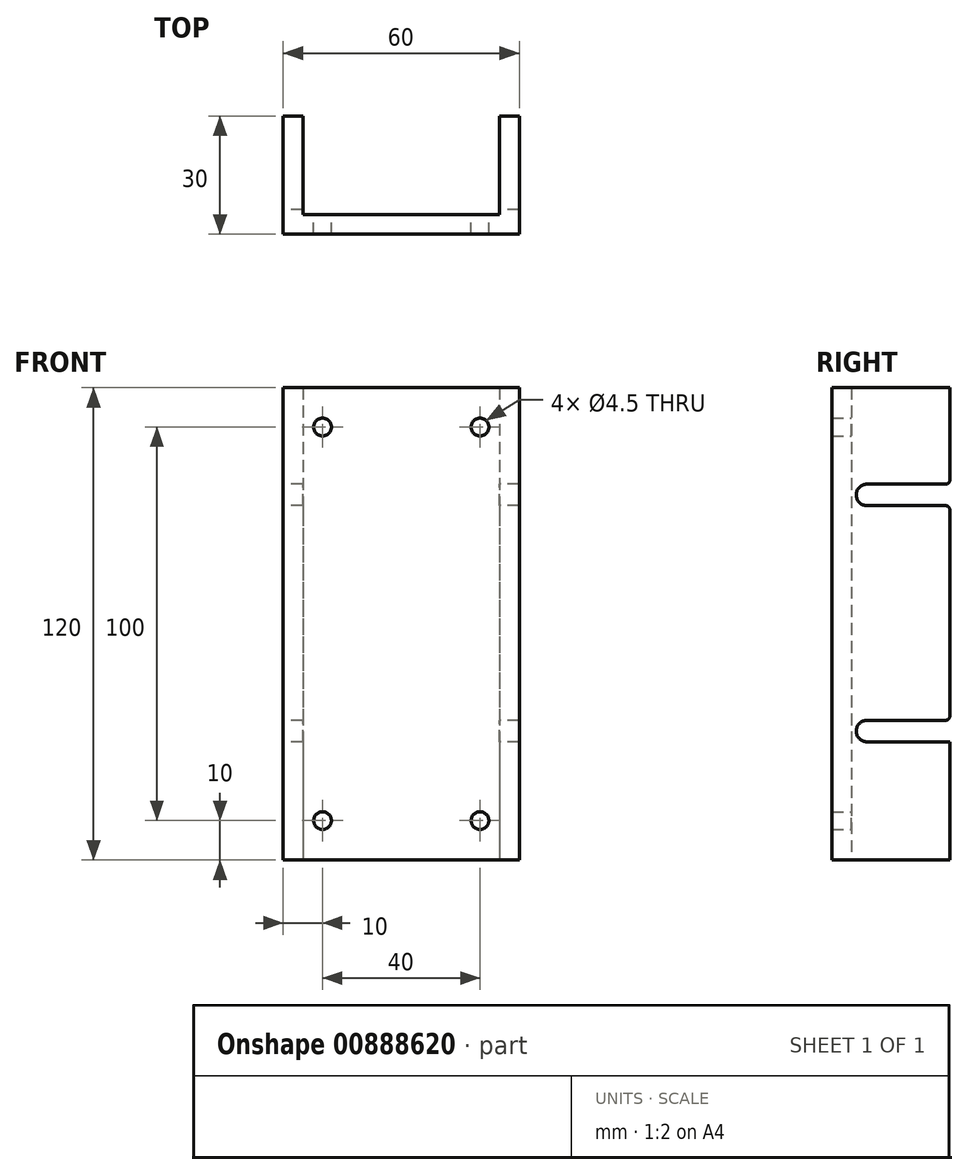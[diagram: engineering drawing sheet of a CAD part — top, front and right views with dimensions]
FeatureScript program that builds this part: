
annotation { "Feature Type Name" : "Feature", "Feature Type Description" : "" }
export const myFeature = defineFeature(function(context is Context, id is Id, definition is map)
    precondition{}
    {
        {
            var Q0;
            Q0=qCreatedBy(makeId("Front.planeOp"),FACE);
            var sketch = newSketch(context, id + "F0", { "sketchPlane" : qUnion([Q0])});
            skLineSegment(sketch, "E0.bottom", {"start": v(30, 60) * mm, "end": v(-30, 60) * mm});
            skLineSegment(sketch, "E0.top", {"start": v(30, -60) * mm, "end": v(-30, -60) * mm});
            skLineSegment(sketch, "E0.left", {"start": v(30, 60) * mm, "end": v(30, -60) * mm});
            skLineSegment(sketch, "E0.right", {"start": v(-30, 60) * mm, "end": v(-30, -60) * mm});
            skPoint(sketch, "E0.middle", {"position": v(0, 0) * mm});
            skLineSegment(sketch, "E1.bottom", {"start": v(-20, 50) * mm, "end": v(20, 50) * mm, "construction": true});
            skLineSegment(sketch, "E1.top", {"start": v(-20, -50) * mm, "end": v(20, -50) * mm, "construction": true});
            skLineSegment(sketch, "E1.left", {"start": v(-20, 50) * mm, "end": v(-20, -50) * mm, "construction": true});
            skLineSegment(sketch, "E1.right", {"start": v(20, 50) * mm, "end": v(20, -50) * mm, "construction": true});
            skCircle(sketch, "E2", {"center": v(20, 50) * mm, "radius": 2.25 * mm});
            skCircle(sketch, "E3", {"center": v(-20, 50) * mm, "radius": 2.25 * mm});
            skCircle(sketch, "E4", {"center": v(-20, -50) * mm, "radius": 2.25 * mm});
            skCircle(sketch, "E5", {"center": v(20, -50) * mm, "radius": 2.25 * mm});
            skSolve(sketch);
        }
        {
            var Q0;
            Q0=makeQuery(id+"F0.imprint","IMPRINT",FACE,{"disambiguationData":[TD([[makeQuery(id+"F0.imprint","IMPRINT",EDGE,{"derivedFrom":sQuery(id+"F0.wireOp",EDGE,"E0.bottom")}),1.0]])]});
            extrude(context, id + "F1", {"entities" : qUnion([Q0]), "depth" : 5 * mm, "offsetDistance" : 25 * mm});
        }
        {
            var Q0;
            Q0=makeQuery(id+"F1.opExtrude","CAP_FACE",FACE,{"disambiguationData":[OSD([sQuery(id+"F0.wireOp",EDGE,"E0.bottom"),sQuery(id+"F0.wireOp",EDGE,"E0.top"),sQuery(id+"F0.wireOp",EDGE,"E0.left"),sQuery(id+"F0.wireOp",EDGE,"E0.right"),sQuery(id+"F0.wireOp",EDGE,"E2"),sQuery(id+"F0.wireOp",EDGE,"E3"),sQuery(id+"F0.wireOp",EDGE,"E4"),sQuery(id+"F0.wireOp",EDGE,"E5")])],"isStart":true});
            var sketch = newSketch(context, id + "F2", { "sketchPlane" : qUnion([Q0])});
            skLineSegment(sketch, "E6.bottom", {"start": v(-30, 60) * mm, "end": v(-25, 60) * mm});
            skLineSegment(sketch, "E6.top", {"start": v(-30, -60) * mm, "end": v(-25, -60) * mm});
            skLineSegment(sketch, "E6.left", {"start": v(-30, 60) * mm, "end": v(-30, -60) * mm});
            skLineSegment(sketch, "E6.right", {"start": v(-25, 60) * mm, "end": v(-25, -60) * mm});
            skLineSegment(sketch, "E7.bottom", {"start": v(30, 60) * mm, "end": v(25, 60) * mm});
            skLineSegment(sketch, "E7.top", {"start": v(30, -60) * mm, "end": v(25, -60) * mm});
            skLineSegment(sketch, "E7.left", {"start": v(30, 60) * mm, "end": v(30, -60) * mm});
            skLineSegment(sketch, "E7.right", {"start": v(25, 60) * mm, "end": v(25, -60) * mm});
            skSolve(sketch);
        }
        {
            var Q0;
            Q0 = qSketchRegion(id + "F2", true);
            extrude(context, id + "F3", {"entities" : qUnion([Q0]), "operationType" : NewBodyOperationType.ADD, "depth" : 25 * mm, "offsetDistance" : 25 * mm});
        }
        {
            var Q0;
            Q0=makeQuery(id+"F3.boolean.opBoolean","MERGE",FACE,{"derivedFrom":[makeQuery(id+"F1.opExtrude","SWEPT_FACE",FACE,{"disambiguationData":[OSD([sQuery(id+"F0.wireOp",EDGE,"E0.right")])]}),makeQuery(id+"F3.opExtrude","SWEPT_FACE",FACE,{"disambiguationData":[OSD([sQuery(id+"F2.wireOp",EDGE,"E7.left")])]})]});
            var sketch = newSketch(context, id + "F4", { "sketchPlane" : qUnion([Q0])});
            skLineSegment(sketch, "E8.bottom", {"start": v(-4, 35.5) * mm, "end": v(-25, 35.5) * mm});
            skLineSegment(sketch, "E8.top", {"start": v(-4, 30) * mm, "end": v(-25, 30) * mm});
            skLineSegment(sketch, "E8.left", {"start": v(-4, 35.5) * mm, "end": v(-4, 30) * mm});
            skLineSegment(sketch, "E8.right", {"start": v(-25, 35.5) * mm, "end": v(-25, 30) * mm});
            skLineSegment(sketch, "E9.bottom", {"start": v(-4, -24.5) * mm, "end": v(-25, -24.5) * mm});
            skLineSegment(sketch, "E9.top", {"start": v(-4, -30) * mm, "end": v(-25, -30) * mm});
            skLineSegment(sketch, "E9.left", {"start": v(-4, -24.5) * mm, "end": v(-4, -30) * mm});
            skLineSegment(sketch, "E9.right", {"start": v(-25, -24.5) * mm, "end": v(-25, -30) * mm});
            skArc(sketch, "E10", {"start": v(-4, 30) * mm, "mid": v(-1.25, 32.75) * mm, "end": v(-4, 35.5) * mm});
            skArc(sketch, "E11", {"start": v(-4, -30) * mm, "mid": v(-1.25, -27.25) * mm, "end": v(-4, -24.5) * mm});
            skSolve(sketch);
        }
        {
            var Q0;
            Q0 = qSketchRegion(id + "F4", true);
            extrude(context, id + "F5", {"entities" : qUnion([Q0]), "operationType" : NewBodyOperationType.REMOVE, "oppositeDirection" : true, "depth" : 72 * mm, "offsetDistance" : 25 * mm});
        }
        {
            var Q0;
            {var subQ0=sQuery(id+"F2.wireOp",EDGE,"E7.left");var subQ1=sQuery(id+"F4.wireOp",EDGE,"E8.bottom");Q0=makeQuery(id+"F5.boolean.opBoolean","COPY",EDGE,{"disambiguationData":[topologyDisambiguationEdgeConnected([makeQuery(id+"F3.opExtrude","CAP_FACE",FACE,{"disambiguationData":[OSD([sQuery(id+"F2.wireOp",EDGE,"E7.bottom"),sQuery(id+"F2.wireOp",EDGE,"E7.top"),subQ0,sQuery(id+"F2.wireOp",EDGE,"E7.right")])],"isStart":false})])],"derivedFrom":makeQuery(id+"F5.opExtrude","SWEPT_EDGE",EDGE,{"disambiguationData":[OSD([subQ0,subQ1,sQuery(id+"F4.wireOp",EDGE,"E8.right")])]})});}
            var Q1;
            {var subQ0=sQuery(id+"F4.wireOp",EDGE,"E8.top");Q1=makeQuery(id+"F5.boolean.opBoolean","COPY",EDGE,{"disambiguationData":[topologyDisambiguationEdgeConnected([makeQuery(id+"F3.opExtrude","CAP_FACE",FACE,{"disambiguationData":[OSD([sQuery(id+"F2.wireOp",EDGE,"E6.bottom"),sQuery(id+"F2.wireOp",EDGE,"E6.top"),sQuery(id+"F2.wireOp",EDGE,"E6.left"),sQuery(id+"F2.wireOp",EDGE,"E6.right")])],"isStart":false})])],"derivedFrom":makeQuery(id+"F5.opExtrude","SWEPT_EDGE",EDGE,{"disambiguationData":[OSD([sQuery(id+"F2.wireOp",EDGE,"E7.left"),subQ0,sQuery(id+"F4.wireOp",EDGE,"E8.right")])]})});}
            var Q2;
            {var subQ0=sQuery(id+"F4.wireOp",EDGE,"E8.bottom");Q2=makeQuery(id+"F5.boolean.opBoolean","COPY",EDGE,{"disambiguationData":[topologyDisambiguationEdgeConnected([makeQuery(id+"F3.opExtrude","CAP_FACE",FACE,{"disambiguationData":[OSD([sQuery(id+"F2.wireOp",EDGE,"E6.bottom"),sQuery(id+"F2.wireOp",EDGE,"E6.top"),sQuery(id+"F2.wireOp",EDGE,"E6.left"),sQuery(id+"F2.wireOp",EDGE,"E6.right")])],"isStart":false})])],"derivedFrom":makeQuery(id+"F5.opExtrude","SWEPT_EDGE",EDGE,{"disambiguationData":[OSD([sQuery(id+"F2.wireOp",EDGE,"E7.left"),subQ0,sQuery(id+"F4.wireOp",EDGE,"E8.right")])]})});}
            var Q3;
            {var subQ0=sQuery(id+"F2.wireOp",EDGE,"E7.left");var subQ1=sQuery(id+"F4.wireOp",EDGE,"E8.top");Q3=makeQuery(id+"F5.boolean.opBoolean","COPY",EDGE,{"disambiguationData":[topologyDisambiguationEdgeConnected([makeQuery(id+"F3.opExtrude","CAP_FACE",FACE,{"disambiguationData":[OSD([sQuery(id+"F2.wireOp",EDGE,"E7.bottom"),sQuery(id+"F2.wireOp",EDGE,"E7.top"),subQ0,sQuery(id+"F2.wireOp",EDGE,"E7.right")])],"isStart":false})])],"derivedFrom":makeQuery(id+"F5.opExtrude","SWEPT_EDGE",EDGE,{"disambiguationData":[OSD([subQ0,subQ1,sQuery(id+"F4.wireOp",EDGE,"E8.right")])]})});}
            var Q4;
            {var subQ0=sQuery(id+"F4.wireOp",EDGE,"E9.bottom");Q4=makeQuery(id+"F5.boolean.opBoolean","COPY",EDGE,{"disambiguationData":[topologyDisambiguationEdgeConnected([makeQuery(id+"F3.opExtrude","CAP_FACE",FACE,{"disambiguationData":[OSD([sQuery(id+"F2.wireOp",EDGE,"E6.bottom"),sQuery(id+"F2.wireOp",EDGE,"E6.top"),sQuery(id+"F2.wireOp",EDGE,"E6.left"),sQuery(id+"F2.wireOp",EDGE,"E6.right")])],"isStart":false})])],"derivedFrom":makeQuery(id+"F5.opExtrude","SWEPT_EDGE",EDGE,{"disambiguationData":[OSD([sQuery(id+"F2.wireOp",EDGE,"E7.left"),subQ0,sQuery(id+"F4.wireOp",EDGE,"E9.right")])]})});}
            var Q5;
            {var subQ0=sQuery(id+"F2.wireOp",EDGE,"E7.left");var subQ1=sQuery(id+"F4.wireOp",EDGE,"E9.bottom");Q5=makeQuery(id+"F5.boolean.opBoolean","COPY",EDGE,{"disambiguationData":[topologyDisambiguationEdgeConnected([makeQuery(id+"F3.opExtrude","CAP_FACE",FACE,{"disambiguationData":[OSD([sQuery(id+"F2.wireOp",EDGE,"E7.bottom"),sQuery(id+"F2.wireOp",EDGE,"E7.top"),subQ0,sQuery(id+"F2.wireOp",EDGE,"E7.right")])],"isStart":false})])],"derivedFrom":makeQuery(id+"F5.opExtrude","SWEPT_EDGE",EDGE,{"disambiguationData":[OSD([subQ0,subQ1,sQuery(id+"F4.wireOp",EDGE,"E9.right")])]})});}
            var Q6;
            {var subQ0=sQuery(id+"F2.wireOp",EDGE,"E7.left");var subQ1=sQuery(id+"F4.wireOp",EDGE,"E9.top");Q6=makeQuery(id+"F5.boolean.opBoolean","COPY",EDGE,{"disambiguationData":[topologyDisambiguationEdgeConnected([makeQuery(id+"F3.opExtrude","CAP_FACE",FACE,{"disambiguationData":[OSD([sQuery(id+"F2.wireOp",EDGE,"E7.bottom"),sQuery(id+"F2.wireOp",EDGE,"E7.top"),subQ0,sQuery(id+"F2.wireOp",EDGE,"E7.right")])],"isStart":false})])],"derivedFrom":makeQuery(id+"F5.opExtrude","SWEPT_EDGE",EDGE,{"disambiguationData":[OSD([subQ0,subQ1,sQuery(id+"F4.wireOp",EDGE,"E9.right")])]})});}
            var Q7;
            {var subQ0=sQuery(id+"F4.wireOp",EDGE,"E9.top");Q7=makeQuery(id+"F5.boolean.opBoolean","COPY",EDGE,{"disambiguationData":[topologyDisambiguationEdgeConnected([makeQuery(id+"F3.opExtrude","CAP_FACE",FACE,{"disambiguationData":[OSD([sQuery(id+"F2.wireOp",EDGE,"E6.bottom"),sQuery(id+"F2.wireOp",EDGE,"E6.top"),sQuery(id+"F2.wireOp",EDGE,"E6.left"),sQuery(id+"F2.wireOp",EDGE,"E6.right")])],"isStart":false})])],"derivedFrom":makeQuery(id+"F5.opExtrude","SWEPT_EDGE",EDGE,{"disambiguationData":[OSD([sQuery(id+"F2.wireOp",EDGE,"E7.left"),subQ0,sQuery(id+"F4.wireOp",EDGE,"E9.right")])]})});}
            fillet(context, id + "F6", {"entities" : qUnion([Q0, Q1, Q2, Q3, Q4, Q5, Q6, Q7]), "tangentPropagation" : true, "radius" : 1 * mm, "defaultsChanged" : false, "vertexSettings" : [], "allowEdgeOverflow" : false});
        }
    });
